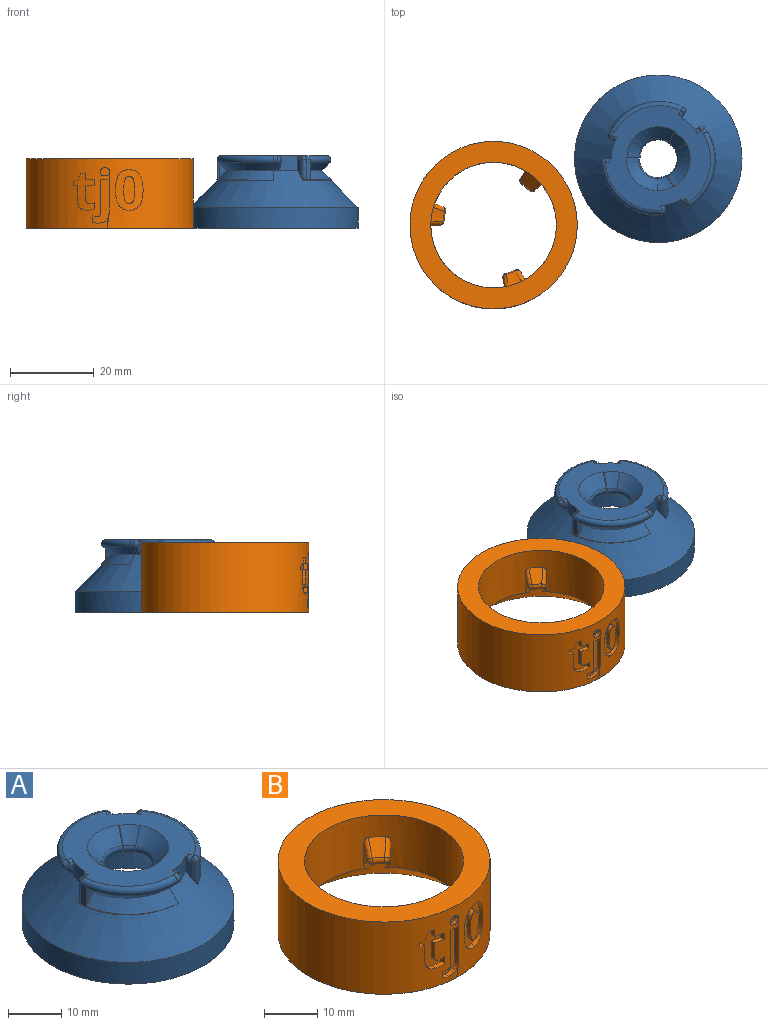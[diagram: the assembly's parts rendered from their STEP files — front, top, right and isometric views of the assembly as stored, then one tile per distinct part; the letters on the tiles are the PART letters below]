
ASSEMBLY  parts=2 mates=1
PART A: 150 faces, bbox 40.3x40.3x23.4 mm
  f0: plane 5.94x2.18mm, normal (0.87,-0.5,0), area 5.6mm2, adj f1,f6,f13,f17,f18,f31,f37,f76
  f1: cylinder r=1mm len=1.47mm, axis (-0.5,-0.87,0), area 1.7mm2, adj f0,f6,f19,f31
  f2: cone r=7.65mm half-angle=45deg, axis (0,0,1), area 39.1mm2, adj f3,f6,f27,f92
  f3: torus R=5.52mm, axis (0,0,1), area 11.4mm2, adj f2,f14,f25,f93
  f4: torus R=12.3mm, axis (0,0,1), area 2.3mm2, adj f5,f6,f9,f30
  f5: cone r=13.01mm half-angle=45deg, axis (0,0,1), area 2.1mm2, adj f4,f10,f13,f28
  f6: plane 25.17x24.95mm, normal (0,0,1), area 285.9mm2, adj f0,f1,f2,f4,f8,f11,f12,f27
  f7: plane 1.08x1mm, normal (-0.37,-0.93,0), area 0.6mm2, adj f8,f10,f11
  f8: cylinder r=1mm len=1.42mm, axis (-0.93,0.37,0), area 1.7mm2, adj f6,f7,f9,f11
  f9: sphere r=1mm, area 1.9mm2, adj f4,f8,f10
  f10: bspline ~10.94x10.14mm, area 3.4mm2, adj f5,f7,f9,f11
  f11: cylinder r=11.18mm len=5.16mm, axis (0,0,1), area 16.5mm2, adj f6,f7,f8,f10,f13,f41
  f12: cone r=7.65mm half-angle=45deg, axis (0,0,1), area 39.1mm2, adj f6,f16,f34,f57
  f13: cone r=11.18mm half-angle=45deg, axis (0,0,-1), area 1025.3mm2, adj f0,f5,f11,f18,f21,f37,f40,f41
  f14: cone r=4.82mm half-angle=45deg, axis (0,0,-1), area 1189.6mm2, adj f3,f15,f16,f22,f23,f26,f48,f53
  f15: cone r=4.82mm half-angle=45deg, axis (0,0,-1), area 0mm2, adj f14,f16,f36
  f16: torus R=5.52mm, axis (0,0,1), area 11.4mm2, adj f12,f14,f15,f35,f55
  f17: cylinder r=1mm len=4.66mm, axis (0,0,1), area 6.8mm2, adj f0,f18,f19,f20
  f18: cone r=11.18mm half-angle=45deg, axis (0,0,-1), area 55.1mm2, adj f0,f13,f17,f20,f28,f29,f32,f33
  f19: sphere r=1mm, area 1.1mm2, adj f1,f17,f30
  f20: cylinder r=13.3mm len=4.66mm, axis (0,0,1), area 5.8mm2, adj f17,f18,f29,f30
  f21: cylinder r=20mm len=40mm, axis (0,0,1), area 628.3mm2, adj f13,f22
  f22: plane 40x40mm, normal (0,0,-1), area 246.8mm2, adj f14,f21
  f23: plane 3.1x0.94mm, normal (0,0,-1), area 0.3mm2, adj f14,f26,f36
  f24: plane 1.12x0.18mm, normal (0,-1,0), area 0mm2, adj f25,f35
  f25: torus R=5.52mm, axis (0,0,1), area 3.5mm2, adj f3,f24,f26,f27,f35
  f26: cone r=4.82mm half-angle=45deg, axis (0,0,-1), area 5.4mm2, adj f14,f23,f25,f35,f36
  f27: cone r=7.65mm half-angle=45deg, axis (0,0,1), area 12.3mm2, adj f2,f6,f25,f34,f35
  f28: cone r=13.01mm half-angle=45deg, axis (0,0,1), area 44mm2, adj f5,f18,f29,f30,f32,f33
  f29: plane 4.66x0.37mm, normal (-0.94,0.34,0), area 1.5mm2, adj f18,f20,f28,f30,f33
  f30: torus R=12.3mm, axis (0,0,1), area 45.2mm2, adj f4,f6,f19,f20,f28,f29
  f31: cylinder r=11.18mm len=1mm, axis (0,0,1), area 0.5mm2, adj f0,f1,f6
  f32: plane 3.46x1.62mm, normal (-0.94,0.34,0), area 3mm2, adj f18,f28,f33
  f33: cylinder r=13.3mm len=3.46mm, axis (0,0,1), area 0.2mm2, adj f18,f28,f29,f32
  f34: bspline ~3.09x3.09mm, area 0.8mm2, adj f6,f12,f27,f35
  f35: bspline ~1.65x0.45mm, area 0.4mm2, adj f16,f24,f25,f26,f27,f34,f36
  f36: bspline ~1.6x1.6mm, area 0.4mm2, adj f15,f23,f26,f35
  f37: cone r=13.7mm half-angle=22.5deg, axis (0,0,1), area 3.2mm2, adj f0,f13,f18
  f38: cylinder r=1mm len=1.13mm, axis (1,0,0), area 1.7mm2, adj f6,f41,f51,f61
  f39: torus R=12.3mm, axis (0,0,1), area 2.3mm2, adj f6,f40,f44,f60
  f40: cone r=13.01mm half-angle=45deg, axis (0,0,1), area 2.1mm2, adj f13,f39,f45,f58
  f41: plane 5.94x2.52mm, normal (0,1,0), area 5.6mm2, adj f6,f11,f13,f38,f49,f50,f61,f67
  f42: plane 1.08x1.07mm, normal (0.99,0.14,0), area 0.6mm2, adj f43,f45,f46
  f43: cylinder r=1mm len=1.25mm, axis (0.14,-0.99,0), area 1.7mm2, adj f6,f42,f44,f46
  f44: sphere r=1mm, area 3mm2, adj f39,f43,f45
  f45: bspline ~10.95x10.94mm, area 3.4mm2, adj f40,f42,f44,f46
  f46: cylinder r=11.18mm len=5.1mm, axis (0,0,1), area 16.5mm2, adj f6,f13,f42,f43,f45,f71
  f47: cone r=7.65mm half-angle=45deg, axis (0,0,1), area 39.1mm2, adj f6,f48,f64,f85
  f48: torus R=5.52mm, axis (0,0,1), area 11.4mm2, adj f14,f47,f65,f83
  f49: cylinder r=1mm len=4.66mm, axis (0,0,1), area 6.8mm2, adj f41,f50,f51,f52
  f50: cone r=11.18mm half-angle=45deg, axis (0,0,-1), area 55.1mm2, adj f13,f41,f49,f52,f58,f59,f62,f63
  f51: sphere r=1mm, area 2.2mm2, adj f38,f49,f60
  f52: cylinder r=13.3mm len=4.66mm, axis (0,0,1), area 5.8mm2, adj f49,f50,f59,f60
  f53: plane 3.16x0.85mm, normal (0,0,-1), area 0.3mm2, adj f14,f56,f66
  f54: plane 1.12x0.15mm, normal (0.87,0.5,0), area 0mm2, adj f55,f65
  f55: torus R=5.52mm, axis (0,0,1), area 3.5mm2, adj f16,f54,f56,f57,f65
  f56: cone r=4.82mm half-angle=45deg, axis (0,0,-1), area 5.4mm2, adj f14,f53,f55,f65,f66
  f57: cone r=7.65mm half-angle=45deg, axis (0,0,1), area 12.3mm2, adj f6,f12,f55,f64,f65
  f58: cone r=13.01mm half-angle=45deg, axis (0,0,1), area 44mm2, adj f40,f50,f59,f60,f62,f63
  f59: plane 4.66x0.39mm, normal (0.17,-0.98,0), area 1.5mm2, adj f50,f52,f58,f60,f63
  f60: torus R=12.3mm, axis (0,0,1), area 45.2mm2, adj f6,f39,f51,f52,f58,f59
  f61: cylinder r=11.18mm len=1mm, axis (0,0,1), area 0.5mm2, adj f6,f38,f41
  f62: plane 3.46x1.7mm, normal (0.17,-0.98,0), area 3mm2, adj f50,f58,f63
  f63: cylinder r=13.3mm len=3.46mm, axis (0,0,1), area 0.2mm2, adj f50,f58,f59,f62
  f64: bspline ~3.09x2.59mm, area 0.8mm2, adj f6,f47,f57,f65
  f65: bspline ~1.65x0.43mm, area 0.4mm2, adj f48,f54,f55,f56,f57,f64,f66
  f66: bspline ~1.6x1.31mm, area 0.4mm2, adj f14,f53,f56,f65
  f67: cone r=13.7mm half-angle=22.5deg, axis (0,0,1), area 3.2mm2, adj f13,f41,f50
  f68: cylinder r=1mm len=1.47mm, axis (-0.5,0.87,0), area 1.7mm2, adj f6,f71,f79,f89
  f69: torus R=12.3mm, axis (0,0,1), area 2.3mm2, adj f6,f70,f74,f88
  f70: cone r=13.01mm half-angle=45deg, axis (0,0,1), area 2.1mm2, adj f13,f69,f75,f86
  f71: plane 5.94x2.18mm, normal (-0.87,-0.5,0), area 5.6mm2, adj f6,f13,f46,f68,f77,f78,f89,f95
  f72: plane 1.08x0.85mm, normal (-0.62,0.79,0), area 0.6mm2, adj f73,f75,f76
  f73: cylinder r=1mm len=1.5mm, axis (0.79,0.62,0), area 1.7mm2, adj f6,f72,f74,f76
  f74: sphere r=1mm, area 3mm2, adj f69,f73,f75
  f75: bspline ~10.94x9.24mm, area 3.4mm2, adj f70,f72,f74,f76
  f76: cylinder r=11.18mm len=3.84mm, axis (0,0,1), area 16.5mm2, adj f0,f6,f13,f72,f73,f75
  f77: cylinder r=1mm len=4.66mm, axis (0,0,1), area 6.8mm2, adj f71,f78,f79,f80
  f78: cone r=11.18mm half-angle=45deg, axis (0,0,-1), area 55.1mm2, adj f13,f71,f77,f80,f86,f87,f90,f91
  f79: sphere r=1mm, area 2.2mm2, adj f68,f77,f88
  f80: cylinder r=13.3mm len=4.66mm, axis (0,0,1), area 5.8mm2, adj f77,f78,f87,f88
  f81: plane 2.36x2.22mm, normal (0,0,-1), area 0.3mm2, adj f14,f84,f94
  f82: plane 1.12x0.15mm, normal (-0.87,0.5,0), area 0mm2, adj f83,f93
  f83: torus R=5.52mm, axis (0,0,1), area 3.5mm2, adj f48,f82,f84,f85,f93
  f84: cone r=4.82mm half-angle=45deg, axis (0,0,-1), area 5.4mm2, adj f14,f81,f83,f93,f94
  f85: cone r=7.65mm half-angle=45deg, axis (0,0,1), area 12.3mm2, adj f6,f47,f83,f92,f93
  f86: cone r=13.01mm half-angle=45deg, axis (0,0,1), area 44mm2, adj f70,f78,f87,f88,f90,f91
  f87: plane 4.66x0.3mm, normal (0.77,0.64,0), area 1.5mm2, adj f78,f80,f86,f88,f91
  f88: torus R=12.3mm, axis (0,0,1), area 45.2mm2, adj f6,f69,f79,f80,f86,f87
  f89: cylinder r=11.18mm len=1mm, axis (0,0,1), area 0.5mm2, adj f6,f68,f71
  f90: plane 3.46x1.32mm, normal (0.77,0.64,0), area 3mm2, adj f78,f86,f91
  f91: cylinder r=13.3mm len=3.46mm, axis (0,0,1), area 0.2mm2, adj f78,f86,f87,f90
  f92: bspline ~3.09x2.76mm, area 0.8mm2, adj f2,f6,f85,f93
  f93: bspline ~1.65x0.57mm, area 0.4mm2, adj f3,f82,f83,f84,f85,f92,f94
  f94: bspline ~1.51x1.38mm, area 0.4mm2, adj f14,f81,f84,f93
  f95: cone r=13.7mm half-angle=22.5deg, axis (0,0,1), area 3.2mm2, adj f13,f71,f78
  f96: cone r=4.82mm half-angle=45deg, axis (0,0,-1), area 27.9mm2, adj f97,f98,f99,f100,f101,f102,f103,f104
  f97: extruded ~1x1mm, area 0.7mm2, adj f14,f96,f98,f112
  f98: extruded ~1.25x1.25mm, area 0.7mm2, adj f14,f96,f97,f99
  f99: plane 3.62x3.27mm, normal (0,-1,0), area 3.7mm2, adj f14,f96,f98,f100
  f100: plane 2.22x1.3mm, normal (0.71,0,0.71), area 2.1mm2, adj f14,f96,f99,f101
  f101: plane 1.88x1.79mm, normal (0,-1,0), area 1.6mm2, adj f14,f96,f100,f102
  f102: plane 2.23x1.38mm, normal (-0.71,0,-0.71), area 2.1mm2, adj f14,f96,f101,f103
  f103: plane 2.04x1.76mm, normal (0,-1,0), area 1.6mm2, adj f14,f96,f102,f104
  f104: plane 1.37x1.31mm, normal (-0.71,0,-0.71), area 1.3mm2, adj f14,f96,f103,f105
  f105: plane 1.91x1.83mm, normal (-0.25,0.94,-0.25), area 1.7mm2, adj f14,f96,f104,f106
  f106: plane 1.64x1.17mm, normal (-0.6,0.52,-0.6), area 1.3mm2, adj f14,f96,f105,f107
  f107: plane 1.47x1.21mm, normal (0,1,0), area 0.9mm2, adj f14,f96,f106,f108
  f108: plane 1.14x1.14mm, normal (0.71,0,0.71), area 1mm2, adj f14,f96,f107,f109
  f109: plane 3.81x3.17mm, normal (0,1,0), area 3.7mm2, adj f14,f96,f108,f110
  f110: extruded ~2.32x2.32mm, area 2mm2, adj f14,f96,f109,f111
  f111: extruded ~1.81x1.59mm, area 2mm2, adj f14,f96,f110,f113
  f112: extruded ~1.31x1.09mm, area 1.3mm2, adj f14,f96,f97,f114
  f113: extruded ~1.91x1.26mm, area 2mm2, adj f14,f96,f111,f114
  f114: plane 1.83x1.79mm, normal (0,-1,0), area 1.5mm2, adj f14,f96,f112,f113
  f115: cone r=4.82mm half-angle=45deg, axis (0,0,-1), area 3.4mm2, adj f116,f117,f118,f119,f120
  f116: extruded ~1.56x1.56mm, area 1.7mm2, adj f14,f115,f117,f118
  f117: extruded ~0.93x0.93mm, area 0.9mm2, adj f14,f115,f116,f119
  f118: extruded ~1.55x1.55mm, area 1.7mm2, adj f14,f115,f116,f120
  f119: extruded ~1.24x1.24mm, area 0.8mm2, adj f14,f115,f117,f120
  f120: extruded ~1.47x1.47mm, area 1.7mm2, adj f14,f115,f118,f119
  f121: cone r=4.82mm half-angle=45deg, axis (0,0,-1), area 25.3mm2, adj f122,f123,f124,f125,f126,f127,f128,f129
  f122: extruded ~1.99x1.28mm, area 2.1mm2, adj f14,f121,f123,f129
  f123: extruded ~2.04x2.04mm, area 2.1mm2, adj f14,f121,f122,f124
  f124: plane 6.69x6.69mm, normal (0,-1,0), area 8.4mm2, adj f14,f121,f123,f125
  f125: plane 2.16x0.92mm, normal (-0.71,0,-0.71), area 2.1mm2, adj f14,f121,f124,f126
  f126: plane 6.77x6.67mm, normal (0,1,0), area 8.1mm2, adj f14,f121,f125,f127
  f127: extruded ~1.33x1.33mm, area 0.9mm2, adj f14,f121,f126,f128
  f128: extruded ~0.98x0.98mm, area 0.8mm2, adj f14,f121,f127,f130
  f129: extruded ~1.37x0.97mm, area 1.4mm2, adj f14,f121,f122,f131
  f130: extruded ~0.97x0.92mm, area 1mm2, adj f14,f121,f128,f131
  f131: plane 1.89x1.85mm, normal (0,1,0), area 1.6mm2, adj f14,f121,f129,f130
  f132: cone r=4.82mm half-angle=45deg, axis (0,0,-1), area 42.6mm2, adj f133,f134,f135,f136,f137,f138,f139,f140
  f133: extruded ~2.69x2.69mm, area 2.7mm2, adj f132,f134,f143,f149
  f134: extruded ~1.57x1.57mm, area 1.4mm2, adj f132,f133,f135,f149
  f135: extruded ~1.55x1.55mm, area 1.4mm2, adj f132,f134,f136,f149
  f136: extruded ~2.64x2.64mm, area 2.7mm2, adj f132,f135,f137,f149
  f137: extruded ~2.77x2.77mm, area 2.6mm2, adj f132,f136,f144,f149
  f138: extruded ~3.52x3.52mm, area 4mm2, adj f14,f132,f139,f146
  f139: extruded ~2.6x2.52mm, area 3mm2, adj f14,f132,f138,f140
  f140: extruded ~2.62x2.26mm, area 3mm2, adj f14,f132,f139,f141
  f141: extruded ~3.57x3.57mm, area 4mm2, adj f14,f132,f140,f142
  f142: extruded ~3.46x3.46mm, area 4mm2, adj f14,f132,f141,f147
  f143: extruded ~2.57x2.57mm, area 2.7mm2, adj f132,f133,f145,f149
  f144: extruded ~1.52x1.52mm, area 1.4mm2, adj f132,f137,f145,f149
  f145: extruded ~1.43x1.43mm, area 1.4mm2, adj f132,f143,f144,f149
  f146: extruded ~4.01x4.01mm, area 4mm2, adj f14,f132,f138,f148
  f147: extruded ~2.6x1.94mm, area 3mm2, adj f14,f132,f142,f148
  f148: extruded ~2.63x2.22mm, area 3mm2, adj f14,f132,f146,f147
  f149: cone r=4.82mm half-angle=45deg, axis (0,0,-1), area 15.8mm2, adj f133,f134,f135,f136,f137,f143,f144,f145
PART B: 90 faces, bbox 40x40x16.7 mm
  f0: plane 4.31x2.16mm, normal (0,-1,0), area 4.7mm2, adj f1,f88,f89
  f1: bspline ~8.57x8.56mm, area 5.6mm2, adj f0,f2,f86,f87,f88
  f2: cone r=12.17mm half-angle=45deg, axis (0,0,-1), area 741.1mm2, adj f1,f3,f11,f12,f13,f21,f22,f23
  f3: bspline ~8.61x8.56mm, area 5.4mm2, adj f2,f4,f10,f88
  f4: plane 4.31x2.13mm, normal (-0.98,-0.17,0), area 4.7mm2, adj f3,f5,f88
  f5: bspline ~8.05x8mm, area 5.4mm2, adj f4,f6,f10,f88
  f6: cone r=15mm half-angle=45deg, axis (0,0,1), area 11.3mm2, adj f5,f7,f11,f88
  f7: bspline ~8.56x7.39mm, area 5.4mm2, adj f6,f8,f9,f88
  f8: plane 4.31x1.87mm, normal (0.87,0.5,0), area 4.7mm2, adj f7,f12,f88
  f9: sphere r=1mm, area 1.5mm2, adj f7,f11,f12
  f10: sphere r=1mm, area 1.5mm2, adj f3,f5,f11
  f11: torus R=12.88mm, axis (0,0,1), area 3.6mm2, adj f2,f6,f9,f10
  f12: bspline ~8.56x7.39mm, area 5.4mm2, adj f2,f8,f9,f88
  f13: bspline ~8x6.74mm, area 5.4mm2, adj f2,f14,f20,f88
  f14: plane 4.31x1.66mm, normal (0.64,-0.77,0), area 4.7mm2, adj f13,f15,f88
  f15: bspline ~8x6.74mm, area 5.4mm2, adj f14,f16,f20,f88
  f16: cone r=15mm half-angle=45deg, axis (0,0,1), area 11.3mm2, adj f15,f17,f21,f88
  f17: bspline ~8.56x7.9mm, area 5.4mm2, adj f16,f18,f19,f88
  f18: plane 4.31x1.87mm, normal (-0.87,0.5,0), area 4.7mm2, adj f17,f22,f88
  f19: sphere r=1mm, area 1.5mm2, adj f17,f21,f22
  f20: sphere r=1mm, area 1.5mm2, adj f13,f15,f21
  f21: torus R=12.88mm, axis (0,0,1), area 3.6mm2, adj f2,f16,f19,f20
  f22: bspline ~8.56x7.9mm, area 5.4mm2, adj f2,f18,f19,f88
  f23: bspline ~8.56x8.02mm, area 5.4mm2, adj f2,f24,f27,f88
  f24: plane 4.31x2.03mm, normal (0.34,0.94,0), area 4.7mm2, adj f23,f25,f88
  f25: bspline ~8x7.49mm, area 5.4mm2, adj f24,f26,f27,f88
  f26: cone r=15mm half-angle=45deg, axis (0,0,1), area 11.3mm2, adj f25,f28,f88,f89
  f27: sphere r=1mm, area 1.5mm2, adj f23,f25,f28
  f28: torus R=12.88mm, axis (0,0,1), area 3.6mm2, adj f2,f26,f27,f87
  f29: plane 40x40mm, normal (0,0,-1), area 49.8mm2, adj f2,f30
  f30: cylinder r=20mm len=40mm, axis (0,0,1), area 1992.5mm2, adj f29,f31,f33,f34,f35,f36,f37,f38
  f31: extruded ~1.07x0.62mm, area 0.7mm2, adj f30,f32,f33,f49
  f32: cylinder r=20mm len=8.9mm, axis (0,0,1), area 24.2mm2, adj f31,f33,f34,f35,f36,f37,f38,f39
  f33: plane 3.48x1mm, normal (-1,0,0), area 3.5mm2, adj f30,f31,f32,f34
  f34: plane 2.02x1.48mm, normal (0,0,1), area 2mm2, adj f30,f32,f33,f35
  f35: plane 1.48x1mm, normal (-1,0,0), area 1.5mm2, adj f30,f32,f34,f36
  f36: plane 2.02x1.48mm, normal (0,0,-1), area 2mm2, adj f30,f32,f35,f37
  f37: plane 1.54x1mm, normal (-1,0,0), area 1.5mm2, adj f30,f32,f36,f38
  f38: plane 1.42x1.26mm, normal (0,0,-1), area 1.3mm2, adj f30,f32,f37,f39
  f39: plane 1.53x1.22mm, normal (0.94,0,-0.35), area 1.6mm2, adj f30,f32,f38,f40
  f40: plane 1.48x1.09mm, normal (0.52,0,-0.85), area 1.3mm2, adj f30,f32,f39,f41
  f41: plane 1x0.83mm, normal (1,0,0), area 0.8mm2, adj f30,f32,f40,f42
  f42: plane 1.42x0.94mm, normal (0,0,1), area 0.9mm2, adj f30,f32,f41,f43
  f43: plane 3.48x1mm, normal (1,0,0), area 3.5mm2, adj f30,f32,f42,f44
  f44: extruded ~1.8x1.21mm, area 1.9mm2, adj f30,f32,f43,f45
  f45: extruded ~1.72x1.56mm, area 1.9mm2, adj f30,f32,f44,f46
  f46: extruded ~1.81x1.41mm, area 1.9mm2, adj f30,f32,f45,f47
  f47: plane 1.47x1mm, normal (-1,0,0), area 1.5mm2, adj f30,f32,f46,f48
  f48: extruded ~1.26x1.24mm, area 1.3mm2, adj f30,f32,f47,f49
  f49: extruded ~1.16x0.63mm, area 0.7mm2, adj f30,f31,f32,f48
  f50: extruded ~1.78x1.02mm, area 2mm2, adj f30,f51,f52,f60
  f51: cylinder r=20mm len=10.41mm, axis (0,0,1), area 22.2mm2, adj f50,f52,f53,f54,f55,f56,f57,f58
  f52: plane 8.01x1mm, normal (-1,0,0), area 8mm2, adj f30,f50,f51,f53
  f53: plane 1.97x1.11mm, normal (0,0,-1), area 2mm2, adj f30,f51,f52,f54
  f54: plane 7.72x1mm, normal (1,0,0), area 7.7mm2, adj f30,f51,f53,f55
  f55: extruded ~1.03x0.82mm, area 0.9mm2, adj f30,f51,f54,f56
  f56: extruded ~1.1x0.73mm, area 0.8mm2, adj f30,f51,f55,f57
  f57: extruded ~1.16x0.93mm, area 0.9mm2, adj f30,f51,f56,f58
  f58: plane 1.55x1mm, normal (1,0,0), area 1.6mm2, adj f30,f51,f57,f59
  f59: extruded ~1.3x1.22mm, area 1.3mm2, adj f30,f51,f58,f60
  f60: extruded ~1.89x1.16mm, area 2mm2, adj f30,f50,f51,f59
  f61: extruded ~1.03x0.81mm, area 0.9mm2, adj f30,f62,f63,f66
  f62: cylinder r=20mm len=2.15mm, axis (0,0,1), area 2.3mm2, adj f61,f63,f64,f65,f66
  f63: extruded ~1x0.72mm, area 0.8mm2, adj f30,f61,f62,f64
  f64: extruded ~1.07x1.03mm, area 1.7mm2, adj f30,f62,f63,f65
  f65: extruded ~1.09x1.07mm, area 1.7mm2, adj f30,f62,f64,f66
  f66: extruded ~1.09x1.07mm, area 1.7mm2, adj f30,f61,f62,f65
  f67: extruded ~2.47x1.77mm, area 2.9mm2, adj f30,f68,f78,f84
  f68: cylinder r=20mm len=9.73mm, axis (0,0,1), area 36.4mm2, adj f67,f69,f71,f72,f73,f74,f75,f76
  f69: extruded ~2.49x1.05mm, area 2.5mm2, adj f68,f70,f71,f77
  f70: cylinder r=20mm len=6.5mm, axis (0,0,1), area 13.5mm2, adj f69,f71,f72,f73,f74,f75,f76,f77
  f71: extruded ~1.22x1.01mm, area 1.4mm2, adj f68,f69,f70,f72
  f72: extruded ~1.27x1.01mm, area 1.4mm2, adj f68,f70,f71,f73
  f73: extruded ~2.48x1.1mm, area 2.5mm2, adj f68,f70,f72,f74
  f74: extruded ~2.5x1.1mm, area 2.5mm2, adj f68,f70,f73,f75
  f75: extruded ~1.27x1.01mm, area 1.3mm2, adj f68,f70,f74,f76
  f76: extruded ~1.22x1.01mm, area 1.4mm2, adj f68,f70,f75,f77
  f77: extruded ~2.5x1.05mm, area 2.5mm2, adj f68,f69,f70,f76
  f78: extruded ~2.49x1.44mm, area 2.9mm2, adj f30,f67,f68,f79
  f79: extruded ~3.69x1.07mm, area 3.8mm2, adj f30,f68,f78,f80
  f80: extruded ~3.63x1.08mm, area 3.8mm2, adj f30,f68,f79,f81
  f81: extruded ~2.47x1.43mm, area 2.9mm2, adj f30,f68,f80,f82
  f82: extruded ~2.5x1.78mm, area 2.9mm2, adj f30,f68,f81,f83
  f83: extruded ~3.67x1.33mm, area 3.8mm2, adj f30,f68,f82,f84
  f84: extruded ~3.64x1.34mm, area 3.8mm2, adj f30,f67,f68,f83
  f85: plane 40x40mm, normal (0,0,1), area 549.8mm2, adj f30,f88
  f86: cone r=12.17mm half-angle=45deg, axis (0,0,-1), area 0mm2, adj f1,f2
  f87: sphere r=1mm, area 1.3mm2, adj f1,f28,f89
  f88: cylinder r=15mm len=30mm, axis (0,0,1), area 1034.5mm2, adj f0,f1,f2,f3,f4,f5,f6,f7
  f89: bspline ~8.57x8.56mm, area 5.4mm2, adj f0,f26,f87,f88
PLACE A t=(27.83,13.99,9.43)mm
PLACE B t=(-11.51,-1.87,3.75)mm fixed
MATE planar B.f2 <-> A.f2  axis (0,0,-1) through (-11.51,-1.87,4.15)mm
